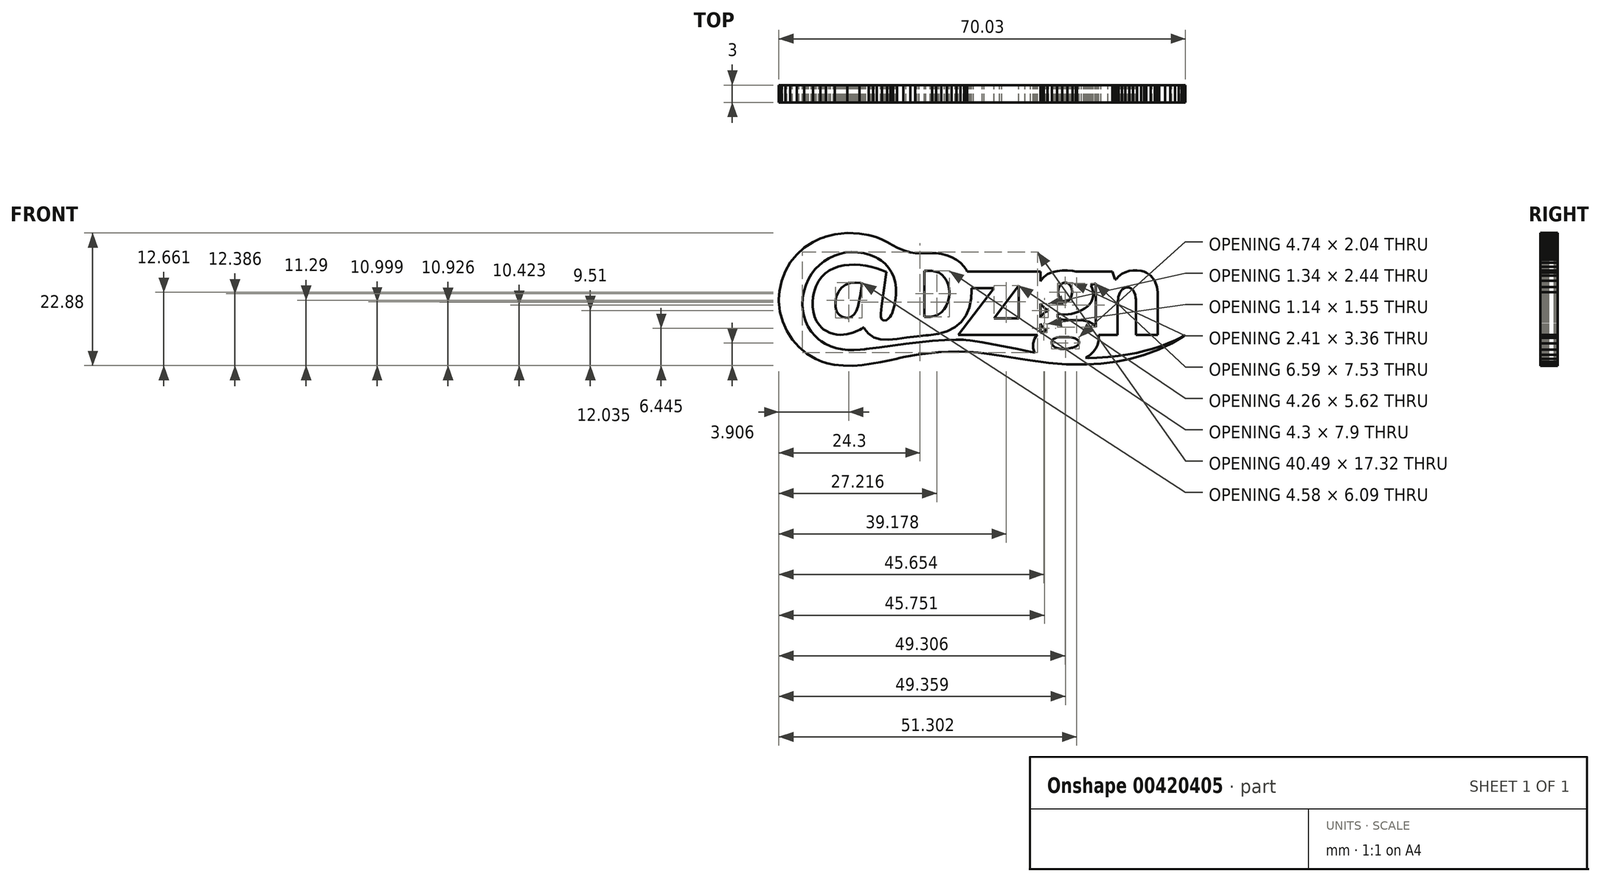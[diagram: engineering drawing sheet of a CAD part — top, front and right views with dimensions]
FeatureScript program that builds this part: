
annotation { "Feature Type Name" : "Feature", "Feature Type Description" : "" }
export const myFeature = defineFeature(function(context is Context, id is Id, definition is map)
    precondition{}
    {
        {
            var Q0;
            Q0=qCreatedBy(makeId("Front.planeOp"),FACE);
            var sketch = newSketch(context, id + "F0", { "sketchPlane" : qUnion([Q0])});
            skLineSegment(sketch, "E0", {"start": v(-17.71, 8.35) * mm, "end": v(-18.04, 6.17) * mm});
            skLineSegment(sketch, "E1", {"start": v(-18.04, 6.17) * mm, "end": v(-18.08, 5.96) * mm});
            skLineSegment(sketch, "E2", {"start": v(-18.08, 5.96) * mm, "end": v(-18.18, 5.3) * mm});
            skLineSegment(sketch, "E3", {"start": v(-18.18, 5.3) * mm, "end": v(-18.4, 4.37) * mm});
            skLineSegment(sketch, "E4", {"start": v(-18.4, 4.37) * mm, "end": v(-18.74, 3.5) * mm});
            skLineSegment(sketch, "E5", {"start": v(-18.74, 3.5) * mm, "end": v(-19.12, 2.94) * mm});
            skLineSegment(sketch, "E6", {"start": v(-19.12, 2.94) * mm, "end": v(-19.29, 2.8) * mm});
            skLineSegment(sketch, "E7", {"start": v(-19.29, 2.8) * mm, "end": v(-19.38, 2.71) * mm});
            skLineSegment(sketch, "E8", {"start": v(-19.38, 2.71) * mm, "end": v(-19.73, 2.52) * mm});
            skLineSegment(sketch, "E9", {"start": v(-19.73, 2.52) * mm, "end": v(-20.2, 2.4) * mm});
            skLineSegment(sketch, "E10", {"start": v(-20.2, 2.4) * mm, "end": v(-20.66, 2.41) * mm});
            skLineSegment(sketch, "E11", {"start": v(-20.66, 2.41) * mm, "end": v(-21.1, 2.55) * mm});
            skLineSegment(sketch, "E12", {"start": v(-21.1, 2.55) * mm, "end": v(-21.5, 2.8) * mm});
            skLineSegment(sketch, "E13", {"start": v(-21.5, 2.8) * mm, "end": v(-21.84, 3.13) * mm});
            skLineSegment(sketch, "E14", {"start": v(-21.84, 3.13) * mm, "end": v(-22.09, 3.55) * mm});
            skLineSegment(sketch, "E15", {"start": v(-22.09, 3.55) * mm, "end": v(-22.21, 3.9) * mm});
            skLineSegment(sketch, "E16", {"start": v(-22.21, 3.9) * mm, "end": v(-22.23, 4.02) * mm});
            skLineSegment(sketch, "E17", {"start": v(-22.23, 4.02) * mm, "end": v(-22.28, 4.28) * mm});
            skLineSegment(sketch, "E18", {"start": v(-22.28, 4.28) * mm, "end": v(-22.3, 5.09) * mm});
            skLineSegment(sketch, "E19", {"start": v(-22.3, 5.09) * mm, "end": v(-22.14, 6.05) * mm});
            skLineSegment(sketch, "E20", {"start": v(-22.14, 6.05) * mm, "end": v(-21.78, 6.88) * mm});
            skLineSegment(sketch, "E21", {"start": v(-21.78, 6.88) * mm, "end": v(-21.24, 7.56) * mm});
            skLineSegment(sketch, "E22", {"start": v(-21.24, 7.56) * mm, "end": v(-20.54, 8.07) * mm});
            skLineSegment(sketch, "E23", {"start": v(-20.54, 8.07) * mm, "end": v(-19.71, 8.38) * mm});
            skLineSegment(sketch, "E24", {"start": v(-19.71, 8.38) * mm, "end": v(-18.76, 8.48) * mm});
            skLineSegment(sketch, "E25", {"start": v(-18.76, 8.48) * mm, "end": v(-17.97, 8.4) * mm});
            skLineSegment(sketch, "E26", {"start": v(-17.97, 8.4) * mm, "end": v(-17.71, 8.35) * mm});
            skLineSegment(sketch, "E27", {"start": v(-16.97, -2.98) * mm, "end": v(-17.23, -3.02) * mm});
            skLineSegment(sketch, "E28", {"start": v(-17.23, -3.02) * mm, "end": v(-18.02, -3.1) * mm});
            skLineSegment(sketch, "E29", {"start": v(-18.02, -3.1) * mm, "end": v(-19.07, -3.14) * mm});
            skLineSegment(sketch, "E30", {"start": v(-19.07, -3.14) * mm, "end": v(-20.11, -3.13) * mm});
            skLineSegment(sketch, "E31", {"start": v(-20.11, -3.13) * mm, "end": v(-21.14, -3.02) * mm});
            skLineSegment(sketch, "E32", {"start": v(-21.14, -3.02) * mm, "end": v(-22.15, -2.82) * mm});
            skLineSegment(sketch, "E33", {"start": v(-22.15, -2.82) * mm, "end": v(-23.13, -2.5) * mm});
            skLineSegment(sketch, "E34", {"start": v(-23.13, -2.5) * mm, "end": v(-24.07, -2.06) * mm});
            skLineSegment(sketch, "E35", {"start": v(-24.07, -2.06) * mm, "end": v(-24.75, -1.64) * mm});
            skLineSegment(sketch, "E36", {"start": v(-24.75, -1.64) * mm, "end": v(-24.97, -1.48) * mm});
            skLineSegment(sketch, "E37", {"start": v(-24.97, -1.48) * mm, "end": v(-25.18, -1.31) * mm});
            skLineSegment(sketch, "E38", {"start": v(-25.18, -1.31) * mm, "end": v(-25.78, -0.77) * mm});
            skLineSegment(sketch, "E39", {"start": v(-25.78, -0.77) * mm, "end": v(-26.46, 0.03) * mm});
            skLineSegment(sketch, "E40", {"start": v(-26.46, 0.03) * mm, "end": v(-27.02, 0.9) * mm});
            skLineSegment(sketch, "E41", {"start": v(-27.02, 0.9) * mm, "end": v(-27.45, 1.83) * mm});
            skLineSegment(sketch, "E42", {"start": v(-27.45, 1.83) * mm, "end": v(-27.76, 2.8) * mm});
            skLineSegment(sketch, "E43", {"start": v(-27.76, 2.8) * mm, "end": v(-27.93, 3.83) * mm});
            skLineSegment(sketch, "E44", {"start": v(-27.93, 3.83) * mm, "end": v(-27.98, 4.88) * mm});
            skLineSegment(sketch, "E45", {"start": v(-27.98, 4.88) * mm, "end": v(-27.94, 5.68) * mm});
            skLineSegment(sketch, "E46", {"start": v(-27.94, 5.68) * mm, "end": v(-27.9, 5.94) * mm});
            skLineSegment(sketch, "E47", {"start": v(-27.9, 5.94) * mm, "end": v(-27.86, 6.22) * mm});
            skLineSegment(sketch, "E48", {"start": v(-27.86, 6.22) * mm, "end": v(-27.69, 7.05) * mm});
            skLineSegment(sketch, "E49", {"start": v(-27.69, 7.05) * mm, "end": v(-27.35, 8.1) * mm});
            skLineSegment(sketch, "E50", {"start": v(-27.35, 8.1) * mm, "end": v(-26.91, 9.08) * mm});
            skLineSegment(sketch, "E51", {"start": v(-26.91, 9.08) * mm, "end": v(-26.38, 9.97) * mm});
            skLineSegment(sketch, "E52", {"start": v(-26.38, 9.97) * mm, "end": v(-25.75, 10.8) * mm});
            skLineSegment(sketch, "E53", {"start": v(-25.75, 10.8) * mm, "end": v(-25.04, 11.52) * mm});
            skLineSegment(sketch, "E54", {"start": v(-25.04, 11.52) * mm, "end": v(-24.25, 12.15) * mm});
            skLineSegment(sketch, "E55", {"start": v(-24.25, 12.15) * mm, "end": v(-23.4, 12.69) * mm});
            skLineSegment(sketch, "E56", {"start": v(-23.4, 12.69) * mm, "end": v(-22.5, 13.12) * mm});
            skLineSegment(sketch, "E57", {"start": v(-22.5, 13.12) * mm, "end": v(-21.54, 13.44) * mm});
            skLineSegment(sketch, "E58", {"start": v(-21.54, 13.44) * mm, "end": v(-20.55, 13.65) * mm});
            skLineSegment(sketch, "E59", {"start": v(-20.55, 13.65) * mm, "end": v(-19.52, 13.74) * mm});
            skLineSegment(sketch, "E60", {"start": v(-19.52, 13.74) * mm, "end": v(-18.47, 13.7) * mm});
            skLineSegment(sketch, "E61", {"start": v(-18.47, 13.7) * mm, "end": v(-17.4, 13.53) * mm});
            skLineSegment(sketch, "E62", {"start": v(-17.4, 13.53) * mm, "end": v(-16.33, 13.23) * mm});
            skLineSegment(sketch, "E63", {"start": v(-16.33, 13.23) * mm, "end": v(-15.52, 12.9) * mm});
            skLineSegment(sketch, "E64", {"start": v(-15.52, 12.9) * mm, "end": v(-15.26, 12.78) * mm});
            skLineSegment(sketch, "E65", {"start": v(-15.26, 12.78) * mm, "end": v(-15.04, 12.68) * mm});
            skLineSegment(sketch, "E66", {"start": v(-15.04, 12.68) * mm, "end": v(-14.42, 12.3) * mm});
            skLineSegment(sketch, "E67", {"start": v(-14.42, 12.3) * mm, "end": v(-13.7, 11.7) * mm});
            skLineSegment(sketch, "E68", {"start": v(-13.7, 11.7) * mm, "end": v(-13.11, 11.02) * mm});
            skLineSegment(sketch, "E69", {"start": v(-13.11, 11.02) * mm, "end": v(-12.63, 10.25) * mm});
            skLineSegment(sketch, "E70", {"start": v(-12.63, 10.25) * mm, "end": v(-12.27, 9.42) * mm});
            skLineSegment(sketch, "E71", {"start": v(-12.27, 9.42) * mm, "end": v(-12.02, 8.54) * mm});
            skLineSegment(sketch, "E72", {"start": v(-12.02, 8.54) * mm, "end": v(-11.88, 7.6) * mm});
            skLineSegment(sketch, "E73", {"start": v(-11.88, 7.6) * mm, "end": v(-11.84, 6.9) * mm});
            skLineSegment(sketch, "E74", {"start": v(-11.84, 6.9) * mm, "end": v(-11.85, 6.65) * mm});
            skLineSegment(sketch, "E75", {"start": v(-11.85, 6.65) * mm, "end": v(-11.86, 6.34) * mm});
            skLineSegment(sketch, "E76", {"start": v(-11.86, 6.34) * mm, "end": v(-12.04, 4.77) * mm});
            skLineSegment(sketch, "E77", {"start": v(-12.04, 4.77) * mm, "end": v(-12.48, 3.24) * mm});
            skLineSegment(sketch, "E78", {"start": v(-12.48, 3.24) * mm, "end": v(-12.62, 2.96) * mm});
            skLineSegment(sketch, "E79", {"start": v(-12.62, 2.96) * mm, "end": v(-12.67, 2.85) * mm});
            skLineSegment(sketch, "E80", {"start": v(-12.67, 2.85) * mm, "end": v(-12.87, 2.55) * mm});
            skLineSegment(sketch, "E81", {"start": v(-12.87, 2.55) * mm, "end": v(-13.17, 2.23) * mm});
            skLineSegment(sketch, "E82", {"start": v(-13.17, 2.23) * mm, "end": v(-13.5, 2.02) * mm});
            skLineSegment(sketch, "E83", {"start": v(-13.5, 2.02) * mm, "end": v(-13.82, 1.93) * mm});
            skLineSegment(sketch, "E84", {"start": v(-13.82, 1.93) * mm, "end": v(-14.1, 1.98) * mm});
            skLineSegment(sketch, "E85", {"start": v(-14.1, 1.98) * mm, "end": v(-14.34, 2.19) * mm});
            skLineSegment(sketch, "E86", {"start": v(-14.34, 2.19) * mm, "end": v(-14.47, 2.56) * mm});
            skLineSegment(sketch, "E87", {"start": v(-14.47, 2.56) * mm, "end": v(-14.5, 2.98) * mm});
            skLineSegment(sketch, "E88", {"start": v(-14.5, 2.98) * mm, "end": v(-14.48, 3.11) * mm});
            skLineSegment(sketch, "E89", {"start": v(-14.48, 3.11) * mm, "end": v(-14.34, 4.43) * mm});
            skLineSegment(sketch, "E90", {"start": v(-14.34, 4.43) * mm, "end": v(-13.52, 10.3) * mm});
            skLineSegment(sketch, "E91", {"start": v(-13.52, 10.3) * mm, "end": v(-13.73, 10.4) * mm});
            skLineSegment(sketch, "E92", {"start": v(-13.73, 10.4) * mm, "end": v(-14.36, 10.64) * mm});
            skLineSegment(sketch, "E93", {"start": v(-14.36, 10.64) * mm, "end": v(-15.24, 10.94) * mm});
            skLineSegment(sketch, "E94", {"start": v(-15.24, 10.94) * mm, "end": v(-16.16, 11.18) * mm});
            skLineSegment(sketch, "E95", {"start": v(-16.16, 11.18) * mm, "end": v(-17.1, 11.37) * mm});
            skLineSegment(sketch, "E96", {"start": v(-17.1, 11.37) * mm, "end": v(-18.04, 11.5) * mm});
            skLineSegment(sketch, "E97", {"start": v(-18.04, 11.5) * mm, "end": v(-19, 11.55) * mm});
            skLineSegment(sketch, "E98", {"start": v(-19, 11.55) * mm, "end": v(-19.93, 11.53) * mm});
            skLineSegment(sketch, "E99", {"start": v(-19.93, 11.53) * mm, "end": v(-20.84, 11.43) * mm});
            skLineSegment(sketch, "E100", {"start": v(-20.84, 11.43) * mm, "end": v(-21.72, 11.23) * mm});
            skLineSegment(sketch, "E101", {"start": v(-21.72, 11.23) * mm, "end": v(-22.56, 10.94) * mm});
            skLineSegment(sketch, "E102", {"start": v(-22.56, 10.94) * mm, "end": v(-23.33, 10.55) * mm});
            skLineSegment(sketch, "E103", {"start": v(-23.33, 10.55) * mm, "end": v(-24.04, 10.05) * mm});
            skLineSegment(sketch, "E104", {"start": v(-24.04, 10.05) * mm, "end": v(-24.68, 9.43) * mm});
            skLineSegment(sketch, "E105", {"start": v(-24.68, 9.43) * mm, "end": v(-25.22, 8.7) * mm});
            skLineSegment(sketch, "E106", {"start": v(-25.22, 8.7) * mm, "end": v(-25.66, 7.83) * mm});
            skLineSegment(sketch, "E107", {"start": v(-25.66, 7.83) * mm, "end": v(-25.92, 7.08) * mm});
            skLineSegment(sketch, "E108", {"start": v(-25.92, 7.08) * mm, "end": v(-25.99, 6.83) * mm});
            skLineSegment(sketch, "E109", {"start": v(-25.99, 6.83) * mm, "end": v(-26.04, 6.62) * mm});
            skLineSegment(sketch, "E110", {"start": v(-26.04, 6.62) * mm, "end": v(-26.15, 6) * mm});
            skLineSegment(sketch, "E111", {"start": v(-26.15, 6) * mm, "end": v(-26.23, 5.15) * mm});
            skLineSegment(sketch, "E112", {"start": v(-26.23, 5.15) * mm, "end": v(-26.22, 4.3) * mm});
            skLineSegment(sketch, "E113", {"start": v(-26.22, 4.3) * mm, "end": v(-26.12, 3.44) * mm});
            skLineSegment(sketch, "E114", {"start": v(-26.12, 3.44) * mm, "end": v(-25.9, 2.62) * mm});
            skLineSegment(sketch, "E115", {"start": v(-25.9, 2.62) * mm, "end": v(-25.56, 1.85) * mm});
            skLineSegment(sketch, "E116", {"start": v(-25.56, 1.85) * mm, "end": v(-25.1, 1.15) * mm});
            skLineSegment(sketch, "E117", {"start": v(-25.1, 1.15) * mm, "end": v(-24.65, 0.68) * mm});
            skLineSegment(sketch, "E118", {"start": v(-24.65, 0.68) * mm, "end": v(-24.49, 0.54) * mm});
            skLineSegment(sketch, "E119", {"start": v(-24.49, 0.54) * mm, "end": v(-24.35, 0.43) * mm});
            skLineSegment(sketch, "E120", {"start": v(-24.35, 0.43) * mm, "end": v(-23.9, 0.13) * mm});
            skLineSegment(sketch, "E121", {"start": v(-23.9, 0.13) * mm, "end": v(-23.3, -0.17) * mm});
            skLineSegment(sketch, "E122", {"start": v(-23.3, -0.17) * mm, "end": v(-22.68, -0.37) * mm});
            skLineSegment(sketch, "E123", {"start": v(-22.68, -0.37) * mm, "end": v(-22.07, -0.49) * mm});
            skLineSegment(sketch, "E124", {"start": v(-22.07, -0.49) * mm, "end": v(-21.47, -0.52) * mm});
            skLineSegment(sketch, "E125", {"start": v(-21.47, -0.52) * mm, "end": v(-20.88, -0.5) * mm});
            skLineSegment(sketch, "E126", {"start": v(-20.88, -0.5) * mm, "end": v(-20.32, -0.42) * mm});
            skLineSegment(sketch, "E127", {"start": v(-20.32, -0.42) * mm, "end": v(-19.78, -0.3) * mm});
            skLineSegment(sketch, "E128", {"start": v(-19.78, -0.3) * mm, "end": v(-19.28, -0.15) * mm});
            skLineSegment(sketch, "E129", {"start": v(-19.28, -0.15) * mm, "end": v(-18.82, 0.02) * mm});
            skLineSegment(sketch, "E130", {"start": v(-18.82, 0.02) * mm, "end": v(-18.42, 0.2) * mm});
            skLineSegment(sketch, "E131", {"start": v(-18.42, 0.2) * mm, "end": v(-18.07, 0.36) * mm});
            skLineSegment(sketch, "E132", {"start": v(-18.07, 0.36) * mm, "end": v(-17.79, 0.51) * mm});
            skLineSegment(sketch, "E133", {"start": v(-17.79, 0.51) * mm, "end": v(-17.58, 0.64) * mm});
            skLineSegment(sketch, "E134", {"start": v(-17.58, 0.64) * mm, "end": v(-17.44, 0.72) * mm});
            skLineSegment(sketch, "E135", {"start": v(-17.44, 0.72) * mm, "end": v(-17.4, 0.75) * mm});
            skLineSegment(sketch, "E136", {"start": v(-17.4, 0.75) * mm, "end": v(-17.25, 0.46) * mm});
            skLineSegment(sketch, "E137", {"start": v(-17.25, 0.46) * mm, "end": v(-16.62, -0.32) * mm});
            skLineSegment(sketch, "E138", {"start": v(-16.62, -0.32) * mm, "end": v(-15.65, -0.98) * mm});
            skLineSegment(sketch, "E139", {"start": v(-15.65, -0.98) * mm, "end": v(-14.5, -1.3) * mm});
            skLineSegment(sketch, "E140", {"start": v(-14.5, -1.3) * mm, "end": v(-13.18, -1.35) * mm});
            skLineSegment(sketch, "E141", {"start": v(-13.18, -1.35) * mm, "end": v(-11.69, -1.23) * mm});
            skLineSegment(sketch, "E142", {"start": v(-11.69, -1.23) * mm, "end": v(-10.03, -1) * mm});
            skLineSegment(sketch, "E143", {"start": v(-10.03, -1) * mm, "end": v(-8.22, -0.77) * mm});
            skLineSegment(sketch, "E144", {"start": v(-8.22, -0.77) * mm, "end": v(-6.74, -0.63) * mm});
            skLineSegment(sketch, "E145", {"start": v(-6.74, -0.63) * mm, "end": v(-6.25, -0.6) * mm});
            skLineSegment(sketch, "E146", {"start": v(-6.25, -0.6) * mm, "end": v(-5.83, -0.57) * mm});
            skLineSegment(sketch, "E147", {"start": v(-5.83, -0.57) * mm, "end": v(-4.55, -0.38) * mm});
            skLineSegment(sketch, "E148", {"start": v(-4.55, -0.38) * mm, "end": v(-3.04, 0.08) * mm});
            skLineSegment(sketch, "E149", {"start": v(-3.04, 0.08) * mm, "end": v(-1.73, 0.76) * mm});
            skLineSegment(sketch, "E150", {"start": v(-1.73, 0.76) * mm, "end": v(-0.65, 1.68) * mm});
            skLineSegment(sketch, "E151", {"start": v(-0.65, 1.68) * mm, "end": v(0.2, 2.81) * mm});
            skLineSegment(sketch, "E152", {"start": v(0.2, 2.81) * mm, "end": v(0.8, 4.16) * mm});
            skLineSegment(sketch, "E153", {"start": v(0.8, 4.16) * mm, "end": v(1.12, 5.73) * mm});
            skLineSegment(sketch, "E154", {"start": v(1.12, 5.73) * mm, "end": v(1.18, 7.06) * mm});
            skLineSegment(sketch, "E155", {"start": v(1.18, 7.06) * mm, "end": v(1.15, 7.5) * mm});
            skLineSegment(sketch, "E156", {"start": v(1.15, 7.5) * mm, "end": v(5.02, 7.5) * mm});
            skLineSegment(sketch, "E157", {"start": v(5.02, 7.5) * mm, "end": v(-1.1, -0.55) * mm});
            skLineSegment(sketch, "E158", {"start": v(-1.1, -0.55) * mm, "end": v(12.5, -0.55) * mm});
            skLineSegment(sketch, "E159", {"start": v(12.5, -0.55) * mm, "end": v(12.35, -0.68) * mm});
            skLineSegment(sketch, "E160", {"start": v(12.35, -0.68) * mm, "end": v(12, -1.2) * mm});
            skLineSegment(sketch, "E161", {"start": v(12, -1.2) * mm, "end": v(11.76, -1.99) * mm});
            skLineSegment(sketch, "E162", {"start": v(11.76, -1.99) * mm, "end": v(11.79, -2.81) * mm});
            skLineSegment(sketch, "E163", {"start": v(11.79, -2.81) * mm, "end": v(11.97, -3.4) * mm});
            skLineSegment(sketch, "E164", {"start": v(11.97, -3.4) * mm, "end": v(12.07, -3.59) * mm});
            skLineSegment(sketch, "E165", {"start": v(12.07, -3.59) * mm, "end": v(11.31, -3.44) * mm});
            skLineSegment(sketch, "E166", {"start": v(11.31, -3.44) * mm, "end": v(9.04, -2.98) * mm});
            skLineSegment(sketch, "E167", {"start": v(9.04, -2.98) * mm, "end": v(5.97, -2.36) * mm});
            skLineSegment(sketch, "E168", {"start": v(5.97, -2.36) * mm, "end": v(2.98, -1.82) * mm});
            skLineSegment(sketch, "E169", {"start": v(2.98, -1.82) * mm, "end": v(0.9, -1.51) * mm});
            skLineSegment(sketch, "E170", {"start": v(0.9, -1.51) * mm, "end": v(0.2, -1.44) * mm});
            skLineSegment(sketch, "E171", {"start": v(0.2, -1.44) * mm, "end": v(-0.23, -1.4) * mm});
            skLineSegment(sketch, "E172", {"start": v(-0.23, -1.4) * mm, "end": v(-1.54, -1.36) * mm});
            skLineSegment(sketch, "E173", {"start": v(-1.54, -1.36) * mm, "end": v(-3.5, -1.41) * mm});
            skLineSegment(sketch, "E174", {"start": v(-3.5, -1.41) * mm, "end": v(-5.6, -1.56) * mm});
            skLineSegment(sketch, "E175", {"start": v(-5.6, -1.56) * mm, "end": v(-7.83, -1.79) * mm});
            skLineSegment(sketch, "E176", {"start": v(-7.83, -1.79) * mm, "end": v(-10.13, -2.07) * mm});
            skLineSegment(sketch, "E177", {"start": v(-10.13, -2.07) * mm, "end": v(-12.45, -2.38) * mm});
            skLineSegment(sketch, "E178", {"start": v(-12.45, -2.38) * mm, "end": v(-14.74, -2.7) * mm});
            skLineSegment(sketch, "E179", {"start": v(-14.74, -2.7) * mm, "end": v(-16.41, -2.91) * mm});
            skLineSegment(sketch, "E180", {"start": v(-16.41, -2.91) * mm, "end": v(-16.97, -2.98) * mm});
            skLineSegment(sketch, "E181", {"start": v(-6.98, 10.49) * mm, "end": v(-5.86, 10.49) * mm});
            skLineSegment(sketch, "E182", {"start": v(-5.86, 10.49) * mm, "end": v(-5.68, 10.49) * mm});
            skLineSegment(sketch, "E183", {"start": v(-5.68, 10.49) * mm, "end": v(-5.1, 10.4) * mm});
            skLineSegment(sketch, "E184", {"start": v(-5.1, 10.4) * mm, "end": v(-4.46, 10.17) * mm});
            skLineSegment(sketch, "E185", {"start": v(-4.46, 10.17) * mm, "end": v(-3.9, 9.8) * mm});
            skLineSegment(sketch, "E186", {"start": v(-3.9, 9.8) * mm, "end": v(-3.46, 9.32) * mm});
            skLineSegment(sketch, "E187", {"start": v(-3.46, 9.32) * mm, "end": v(-3.12, 8.75) * mm});
            skLineSegment(sketch, "E188", {"start": v(-3.12, 8.75) * mm, "end": v(-2.87, 8.1) * mm});
            skLineSegment(sketch, "E189", {"start": v(-2.87, 8.1) * mm, "end": v(-2.72, 7.42) * mm});
            skLineSegment(sketch, "E190", {"start": v(-2.72, 7.42) * mm, "end": v(-2.67, 6.9) * mm});
            skLineSegment(sketch, "E191", {"start": v(-2.67, 6.9) * mm, "end": v(-2.67, 6.71) * mm});
            skLineSegment(sketch, "E192", {"start": v(-2.67, 6.71) * mm, "end": v(-2.67, 6.52) * mm});
            skLineSegment(sketch, "E193", {"start": v(-2.67, 6.52) * mm, "end": v(-2.73, 5.95) * mm});
            skLineSegment(sketch, "E194", {"start": v(-2.73, 5.95) * mm, "end": v(-2.9, 5.21) * mm});
            skLineSegment(sketch, "E195", {"start": v(-2.9, 5.21) * mm, "end": v(-3.16, 4.52) * mm});
            skLineSegment(sketch, "E196", {"start": v(-3.16, 4.52) * mm, "end": v(-3.54, 3.89) * mm});
            skLineSegment(sketch, "E197", {"start": v(-3.54, 3.89) * mm, "end": v(-4.03, 3.36) * mm});
            skLineSegment(sketch, "E198", {"start": v(-4.03, 3.36) * mm, "end": v(-4.63, 2.94) * mm});
            skLineSegment(sketch, "E199", {"start": v(-4.63, 2.94) * mm, "end": v(-5.33, 2.68) * mm});
            skLineSegment(sketch, "E200", {"start": v(-5.33, 2.68) * mm, "end": v(-5.93, 2.58) * mm});
            skLineSegment(sketch, "E201", {"start": v(-5.93, 2.58) * mm, "end": v(-6.13, 2.58) * mm});
            skLineSegment(sketch, "E202", {"start": v(-6.13, 2.58) * mm, "end": v(-6.98, 2.58) * mm});
            skLineSegment(sketch, "E203", {"start": v(-6.98, 2.58) * mm, "end": v(-6.98, 10.49) * mm});
            skLineSegment(sketch, "E204", {"start": v(9.27, 2.34) * mm, "end": v(5, 2.34) * mm});
            skLineSegment(sketch, "E205", {"start": v(5, 2.34) * mm, "end": v(9.27, 7.96) * mm});
            skLineSegment(sketch, "E206", {"start": v(9.27, 7.96) * mm, "end": v(9.27, 2.34) * mm});
            skLineSegment(sketch, "E207", {"start": v(13.1, 4.78) * mm, "end": v(13.31, 4.5) * mm});
            skLineSegment(sketch, "E208", {"start": v(13.31, 4.5) * mm, "end": v(13.62, 4.19) * mm});
            skLineSegment(sketch, "E209", {"start": v(13.62, 4.19) * mm, "end": v(13.98, 3.92) * mm});
            skLineSegment(sketch, "E210", {"start": v(13.98, 3.92) * mm, "end": v(14.28, 3.75) * mm});
            skLineSegment(sketch, "E211", {"start": v(14.28, 3.75) * mm, "end": v(14.38, 3.7) * mm});
            skLineSegment(sketch, "E212", {"start": v(14.38, 3.7) * mm, "end": v(14.28, 3.65) * mm});
            skLineSegment(sketch, "E213", {"start": v(14.28, 3.65) * mm, "end": v(13.99, 3.46) * mm});
            skLineSegment(sketch, "E214", {"start": v(13.99, 3.46) * mm, "end": v(13.6, 3.18) * mm});
            skLineSegment(sketch, "E215", {"start": v(13.6, 3.18) * mm, "end": v(13.27, 2.85) * mm});
            skLineSegment(sketch, "E216", {"start": v(13.27, 2.85) * mm, "end": v(13.08, 2.55) * mm});
            skLineSegment(sketch, "E217", {"start": v(13.08, 2.55) * mm, "end": v(13.04, 2.44) * mm});
            skLineSegment(sketch, "E218", {"start": v(13.04, 2.44) * mm, "end": v(13.04, 4.88) * mm});
            skLineSegment(sketch, "E219", {"start": v(15.42, -1.16) * mm, "end": v(15.81, -1) * mm});
            skLineSegment(sketch, "E220", {"start": v(15.81, -1) * mm, "end": v(16.24, -0.92) * mm});
            skLineSegment(sketch, "E221", {"start": v(16.24, -0.92) * mm, "end": v(16.38, -0.92) * mm});
            skLineSegment(sketch, "E222", {"start": v(16.38, -0.92) * mm, "end": v(17.86, -0.92) * mm});
            skLineSegment(sketch, "E223", {"start": v(17.86, -0.92) * mm, "end": v(18, -0.92) * mm});
            skLineSegment(sketch, "E224", {"start": v(18, -0.92) * mm, "end": v(18.44, -0.98) * mm});
            skLineSegment(sketch, "E225", {"start": v(18.44, -0.98) * mm, "end": v(18.95, -1.13) * mm});
            skLineSegment(sketch, "E226", {"start": v(18.95, -1.13) * mm, "end": v(19.35, -1.35) * mm});
            skLineSegment(sketch, "E227", {"start": v(19.35, -1.35) * mm, "end": v(19.6, -1.62) * mm});
            skLineSegment(sketch, "E228", {"start": v(19.6, -1.62) * mm, "end": v(19.7, -1.92) * mm});
            skLineSegment(sketch, "E229", {"start": v(19.7, -1.92) * mm, "end": v(19.56, -2.22) * mm});
            skLineSegment(sketch, "E230", {"start": v(19.56, -2.22) * mm, "end": v(19.19, -2.5) * mm});
            skLineSegment(sketch, "E231", {"start": v(19.19, -2.5) * mm, "end": v(18.7, -2.7) * mm});
            skLineSegment(sketch, "E232", {"start": v(18.7, -2.7) * mm, "end": v(18.53, -2.75) * mm});
            skLineSegment(sketch, "E233", {"start": v(18.53, -2.75) * mm, "end": v(18.37, -2.8) * mm});
            skLineSegment(sketch, "E234", {"start": v(18.37, -2.8) * mm, "end": v(17.87, -2.9) * mm});
            skLineSegment(sketch, "E235", {"start": v(17.87, -2.9) * mm, "end": v(17.17, -2.96) * mm});
            skLineSegment(sketch, "E236", {"start": v(17.17, -2.96) * mm, "end": v(16.47, -2.94) * mm});
            skLineSegment(sketch, "E237", {"start": v(16.47, -2.94) * mm, "end": v(15.97, -2.86) * mm});
            skLineSegment(sketch, "E238", {"start": v(15.97, -2.86) * mm, "end": v(15.8, -2.81) * mm});
            skLineSegment(sketch, "E239", {"start": v(15.8, -2.81) * mm, "end": v(15.74, -2.8) * mm});
            skLineSegment(sketch, "E240", {"start": v(15.74, -2.8) * mm, "end": v(15.54, -2.7) * mm});
            skLineSegment(sketch, "E241", {"start": v(15.54, -2.7) * mm, "end": v(15.3, -2.54) * mm});
            skLineSegment(sketch, "E242", {"start": v(15.3, -2.54) * mm, "end": v(15.12, -2.35) * mm});
            skLineSegment(sketch, "E243", {"start": v(15.12, -2.35) * mm, "end": v(15, -2.13) * mm});
            skLineSegment(sketch, "E244", {"start": v(15, -2.13) * mm, "end": v(14.95, -1.9) * mm});
            skLineSegment(sketch, "E245", {"start": v(14.95, -1.9) * mm, "end": v(14.98, -1.66) * mm});
            skLineSegment(sketch, "E246", {"start": v(14.98, -1.66) * mm, "end": v(15.1, -1.42) * mm});
            skLineSegment(sketch, "E247", {"start": v(15.1, -1.42) * mm, "end": v(15.28, -1.25) * mm});
            skLineSegment(sketch, "E248", {"start": v(16.08, 3.07) * mm, "end": v(16.21, 3.05) * mm});
            skLineSegment(sketch, "E249", {"start": v(16.21, 3.05) * mm, "end": v(16.61, 3) * mm});
            skLineSegment(sketch, "E250", {"start": v(16.61, 3) * mm, "end": v(17.18, 2.97) * mm});
            skLineSegment(sketch, "E251", {"start": v(17.18, 2.97) * mm, "end": v(17.77, 3) * mm});
            skLineSegment(sketch, "E252", {"start": v(17.77, 3) * mm, "end": v(18.37, 3.1) * mm});
            skLineSegment(sketch, "E253", {"start": v(18.37, 3.1) * mm, "end": v(18.97, 3.25) * mm});
            skLineSegment(sketch, "E254", {"start": v(18.97, 3.25) * mm, "end": v(19.55, 3.45) * mm});
            skLineSegment(sketch, "E255", {"start": v(19.55, 3.45) * mm, "end": v(20.1, 3.7) * mm});
            skLineSegment(sketch, "E256", {"start": v(20.1, 3.7) * mm, "end": v(20.62, 4) * mm});
            skLineSegment(sketch, "E257", {"start": v(20.62, 4) * mm, "end": v(21.08, 4.35) * mm});
            skLineSegment(sketch, "E258", {"start": v(21.08, 4.35) * mm, "end": v(21.47, 4.75) * mm});
            skLineSegment(sketch, "E259", {"start": v(21.47, 4.75) * mm, "end": v(21.78, 5.2) * mm});
            skLineSegment(sketch, "E260", {"start": v(21.78, 5.2) * mm, "end": v(22, 5.68) * mm});
            skLineSegment(sketch, "E261", {"start": v(22, 5.68) * mm, "end": v(22.11, 6.2) * mm});
            skLineSegment(sketch, "E262", {"start": v(22.11, 6.2) * mm, "end": v(22.1, 6.77) * mm});
            skLineSegment(sketch, "E263", {"start": v(22.1, 6.77) * mm, "end": v(21.97, 7.37) * mm});
            skLineSegment(sketch, "E264", {"start": v(21.97, 7.37) * mm, "end": v(21.76, 7.86) * mm});
            skLineSegment(sketch, "E265", {"start": v(21.76, 7.86) * mm, "end": v(21.68, 8) * mm});
            skLineSegment(sketch, "E266", {"start": v(21.68, 8) * mm, "end": v(22.56, 8.34) * mm});
            skLineSegment(sketch, "E267", {"start": v(22.56, 8.34) * mm, "end": v(22.56, 0.8) * mm});
            skLineSegment(sketch, "E268", {"start": v(22.56, 0.8) * mm, "end": v(22.45, 0.96) * mm});
            skLineSegment(sketch, "E269", {"start": v(22.45, 0.96) * mm, "end": v(22.04, 1.34) * mm});
            skLineSegment(sketch, "E270", {"start": v(22.04, 1.34) * mm, "end": v(21.34, 1.72) * mm});
            skLineSegment(sketch, "E271", {"start": v(21.34, 1.72) * mm, "end": v(20.46, 1.95) * mm});
            skLineSegment(sketch, "E272", {"start": v(20.46, 1.95) * mm, "end": v(19.66, 2.02) * mm});
            skLineSegment(sketch, "E273", {"start": v(19.66, 2.02) * mm, "end": v(19.4, 2.02) * mm});
            skLineSegment(sketch, "E274", {"start": v(19.4, 2.02) * mm, "end": v(17.58, 2.02) * mm});
            skLineSegment(sketch, "E275", {"start": v(17.58, 2.02) * mm, "end": v(17.51, 2.02) * mm});
            skLineSegment(sketch, "E276", {"start": v(17.51, 2.02) * mm, "end": v(17.32, 2.03) * mm});
            skLineSegment(sketch, "E277", {"start": v(17.32, 2.03) * mm, "end": v(17, 2.05) * mm});
            skLineSegment(sketch, "E278", {"start": v(17, 2.05) * mm, "end": v(16.7, 2.1) * mm});
            skLineSegment(sketch, "E279", {"start": v(16.7, 2.1) * mm, "end": v(16.4, 2.17) * mm});
            skLineSegment(sketch, "E280", {"start": v(16.4, 2.17) * mm, "end": v(16.15, 2.3) * mm});
            skLineSegment(sketch, "E281", {"start": v(16.15, 2.3) * mm, "end": v(16, 2.49) * mm});
            skLineSegment(sketch, "E282", {"start": v(16, 2.49) * mm, "end": v(15.97, 2.74) * mm});
            skLineSegment(sketch, "E283", {"start": v(15.97, 2.74) * mm, "end": v(16.04, 3) * mm});
            skLineSegment(sketch, "E284", {"start": v(16.04, 3) * mm, "end": v(16.08, 3.07) * mm});
            skLineSegment(sketch, "E285", {"start": v(17.29, 8.49) * mm, "end": v(17.42, 8.49) * mm});
            skLineSegment(sketch, "E286", {"start": v(17.42, 8.49) * mm, "end": v(17.8, 8.34) * mm});
            skLineSegment(sketch, "E287", {"start": v(17.8, 8.34) * mm, "end": v(18.18, 7.96) * mm});
            skLineSegment(sketch, "E288", {"start": v(18.18, 7.96) * mm, "end": v(18.4, 7.43) * mm});
            skLineSegment(sketch, "E289", {"start": v(18.4, 7.43) * mm, "end": v(18.47, 6.81) * mm});
            skLineSegment(sketch, "E290", {"start": v(18.47, 6.81) * mm, "end": v(18.4, 6.2) * mm});
            skLineSegment(sketch, "E291", {"start": v(18.4, 6.2) * mm, "end": v(18.17, 5.66) * mm});
            skLineSegment(sketch, "E292", {"start": v(18.17, 5.66) * mm, "end": v(17.8, 5.28) * mm});
            skLineSegment(sketch, "E293", {"start": v(17.8, 5.28) * mm, "end": v(17.41, 5.13) * mm});
            skLineSegment(sketch, "E294", {"start": v(17.41, 5.13) * mm, "end": v(17.29, 5.13) * mm});
            skLineSegment(sketch, "E295", {"start": v(17.29, 5.13) * mm, "end": v(17.15, 5.13) * mm});
            skLineSegment(sketch, "E296", {"start": v(17.15, 5.13) * mm, "end": v(16.75, 5.27) * mm});
            skLineSegment(sketch, "E297", {"start": v(16.75, 5.27) * mm, "end": v(16.37, 5.65) * mm});
            skLineSegment(sketch, "E298", {"start": v(16.37, 5.65) * mm, "end": v(16.14, 6.2) * mm});
            skLineSegment(sketch, "E299", {"start": v(16.14, 6.2) * mm, "end": v(16.06, 6.8) * mm});
            skLineSegment(sketch, "E300", {"start": v(16.06, 6.8) * mm, "end": v(16.14, 7.42) * mm});
            skLineSegment(sketch, "E301", {"start": v(16.14, 7.42) * mm, "end": v(16.37, 7.96) * mm});
            skLineSegment(sketch, "E302", {"start": v(16.37, 7.96) * mm, "end": v(16.75, 8.34) * mm});
            skLineSegment(sketch, "E303", {"start": v(16.75, 8.34) * mm, "end": v(17.15, 8.49) * mm});
            skLineSegment(sketch, "E304", {"start": v(17.15, 8.49) * mm, "end": v(17.29, 8.49) * mm});
            skLineSegment(sketch, "E305", {"start": v(13.04, 1.37) * mm, "end": v(13.08, 1.28) * mm});
            skLineSegment(sketch, "E306", {"start": v(13.08, 1.28) * mm, "end": v(13.24, 1.01) * mm});
            skLineSegment(sketch, "E307", {"start": v(13.24, 1.01) * mm, "end": v(13.5, 0.7) * mm});
            skLineSegment(sketch, "E308", {"start": v(13.5, 0.7) * mm, "end": v(13.82, 0.44) * mm});
            skLineSegment(sketch, "E309", {"start": v(13.82, 0.44) * mm, "end": v(14.1, 0.28) * mm});
            skLineSegment(sketch, "E310", {"start": v(14.1, 0.28) * mm, "end": v(14.19, 0.24) * mm});
            skLineSegment(sketch, "E311", {"start": v(14.19, 0.24) * mm, "end": v(14.08, 0.21) * mm});
            skLineSegment(sketch, "E312", {"start": v(14.08, 0.21) * mm, "end": v(13.57, 0.06) * mm});
            skLineSegment(sketch, "E313", {"start": v(13.57, 0.06) * mm, "end": v(13.12, -0.14) * mm});
            skLineSegment(sketch, "E314", {"start": v(13.12, -0.14) * mm, "end": v(13.04, -0.18) * mm});
            skLineSegment(sketch, "E315", {"start": v(13.04, -0.18) * mm, "end": v(13.04, 1.37) * mm});
            skLineSegment(sketch, "E316", {"start": v(23.04, -0.55) * mm, "end": v(26.33, -0.55) * mm});
            skLineSegment(sketch, "E317", {"start": v(26.33, -0.55) * mm, "end": v(26.33, 4.24) * mm});
            skLineSegment(sketch, "E318", {"start": v(26.33, 4.24) * mm, "end": v(26.33, 4.44) * mm});
            skLineSegment(sketch, "E319", {"start": v(26.33, 4.44) * mm, "end": v(26.34, 5.07) * mm});
            skLineSegment(sketch, "E320", {"start": v(26.34, 5.07) * mm, "end": v(26.44, 5.98) * mm});
            skLineSegment(sketch, "E321", {"start": v(26.44, 5.98) * mm, "end": v(26.73, 6.82) * mm});
            skLineSegment(sketch, "E322", {"start": v(26.73, 6.82) * mm, "end": v(27.14, 7.32) * mm});
            skLineSegment(sketch, "E323", {"start": v(27.14, 7.32) * mm, "end": v(27.31, 7.42) * mm});
            skLineSegment(sketch, "E324", {"start": v(27.31, 7.42) * mm, "end": v(27.43, 7.49) * mm});
            skLineSegment(sketch, "E325", {"start": v(27.43, 7.49) * mm, "end": v(27.84, 7.63) * mm});
            skLineSegment(sketch, "E326", {"start": v(27.84, 7.63) * mm, "end": v(28.3, 7.63) * mm});
            skLineSegment(sketch, "E327", {"start": v(28.3, 7.63) * mm, "end": v(28.66, 7.48) * mm});
            skLineSegment(sketch, "E328", {"start": v(28.66, 7.48) * mm, "end": v(28.95, 7.19) * mm});
            skLineSegment(sketch, "E329", {"start": v(28.95, 7.19) * mm, "end": v(29.18, 6.8) * mm});
            skLineSegment(sketch, "E330", {"start": v(29.18, 6.8) * mm, "end": v(29.33, 6.36) * mm});
            skLineSegment(sketch, "E331", {"start": v(29.33, 6.36) * mm, "end": v(29.42, 5.88) * mm});
            skLineSegment(sketch, "E332", {"start": v(29.42, 5.88) * mm, "end": v(29.45, 5.53) * mm});
            skLineSegment(sketch, "E333", {"start": v(29.45, 5.53) * mm, "end": v(29.45, 5.4) * mm});
            skLineSegment(sketch, "E334", {"start": v(29.45, 5.4) * mm, "end": v(29.45, -0.56) * mm});
            skLineSegment(sketch, "E335", {"start": v(29.45, -0.56) * mm, "end": v(33.23, -0.56) * mm});
            skLineSegment(sketch, "E336", {"start": v(33.23, -0.56) * mm, "end": v(33.23, 6.55) * mm});
            skLineSegment(sketch, "E337", {"start": v(33.23, 6.55) * mm, "end": v(33.23, 6.84) * mm});
            skLineSegment(sketch, "E338", {"start": v(33.23, 6.84) * mm, "end": v(33.1, 7.73) * mm});
            skLineSegment(sketch, "E339", {"start": v(33.1, 7.73) * mm, "end": v(32.7, 8.8) * mm});
            skLineSegment(sketch, "E340", {"start": v(32.7, 8.8) * mm, "end": v(32.02, 9.7) * mm});
            skLineSegment(sketch, "E341", {"start": v(32.02, 9.7) * mm, "end": v(31.27, 10.2) * mm});
            skLineSegment(sketch, "E342", {"start": v(31.27, 10.2) * mm, "end": v(31, 10.3) * mm});
            skLineSegment(sketch, "E343", {"start": v(31, 10.3) * mm, "end": v(30.85, 10.36) * mm});
            skLineSegment(sketch, "E344", {"start": v(30.85, 10.36) * mm, "end": v(30.37, 10.49) * mm});
            skLineSegment(sketch, "E345", {"start": v(30.37, 10.49) * mm, "end": v(29.69, 10.58) * mm});
            skLineSegment(sketch, "E346", {"start": v(29.69, 10.58) * mm, "end": v(29, 10.57) * mm});
            skLineSegment(sketch, "E347", {"start": v(29, 10.57) * mm, "end": v(28.3, 10.47) * mm});
            skLineSegment(sketch, "E348", {"start": v(28.3, 10.47) * mm, "end": v(27.64, 10.27) * mm});
            skLineSegment(sketch, "E349", {"start": v(27.64, 10.27) * mm, "end": v(27.04, 9.96) * mm});
            skLineSegment(sketch, "E350", {"start": v(27.04, 9.96) * mm, "end": v(26.51, 9.55) * mm});
            skLineSegment(sketch, "E351", {"start": v(26.51, 9.55) * mm, "end": v(26.18, 9.16) * mm});
            skLineSegment(sketch, "E352", {"start": v(26.18, 9.16) * mm, "end": v(26.09, 9.02) * mm});
            skLineSegment(sketch, "E353", {"start": v(26.09, 9.02) * mm, "end": v(25.86, 9.02) * mm});
            skLineSegment(sketch, "E354", {"start": v(25.86, 9.02) * mm, "end": v(25.4, 10.37) * mm});
            skLineSegment(sketch, "E355", {"start": v(25.4, 10.37) * mm, "end": v(19.35, 10.37) * mm});
            skLineSegment(sketch, "E356", {"start": v(19.35, 10.37) * mm, "end": v(19.14, 10.4) * mm});
            skLineSegment(sketch, "E357", {"start": v(19.14, 10.4) * mm, "end": v(18.53, 10.48) * mm});
            skLineSegment(sketch, "E358", {"start": v(18.53, 10.48) * mm, "end": v(17.66, 10.55) * mm});
            skLineSegment(sketch, "E359", {"start": v(17.66, 10.55) * mm, "end": v(16.76, 10.56) * mm});
            skLineSegment(sketch, "E360", {"start": v(16.76, 10.56) * mm, "end": v(15.87, 10.47) * mm});
            skLineSegment(sketch, "E361", {"start": v(15.87, 10.47) * mm, "end": v(15.03, 10.26) * mm});
            skLineSegment(sketch, "E362", {"start": v(15.03, 10.26) * mm, "end": v(14.25, 9.92) * mm});
            skLineSegment(sketch, "E363", {"start": v(14.25, 9.92) * mm, "end": v(13.57, 9.42) * mm});
            skLineSegment(sketch, "E364", {"start": v(13.57, 9.42) * mm, "end": v(13.13, 8.92) * mm});
            skLineSegment(sketch, "E365", {"start": v(13.13, 8.92) * mm, "end": v(13.02, 8.73) * mm});
            skLineSegment(sketch, "E366", {"start": v(13.02, 8.73) * mm, "end": v(13.02, 10.37) * mm});
            skLineSegment(sketch, "E367", {"start": v(13.02, 10.37) * mm, "end": v(0.42, 10.37) * mm});
            skLineSegment(sketch, "E368", {"start": v(0.42, 10.37) * mm, "end": v(0.3, 10.58) * mm});
            skLineSegment(sketch, "E369", {"start": v(0.3, 10.58) * mm, "end": v(-0.1, 11.18) * mm});
            skLineSegment(sketch, "E370", {"start": v(-0.1, 11.18) * mm, "end": v(-0.74, 11.87) * mm});
            skLineSegment(sketch, "E371", {"start": v(-0.74, 11.87) * mm, "end": v(-1.46, 12.42) * mm});
            skLineSegment(sketch, "E372", {"start": v(-1.46, 12.42) * mm, "end": v(-2.27, 12.85) * mm});
            skLineSegment(sketch, "E373", {"start": v(-2.27, 12.85) * mm, "end": v(-3.13, 13.17) * mm});
            skLineSegment(sketch, "E374", {"start": v(-3.13, 13.17) * mm, "end": v(-4.04, 13.4) * mm});
            skLineSegment(sketch, "E375", {"start": v(-4.04, 13.4) * mm, "end": v(-4.97, 13.52) * mm});
            skLineSegment(sketch, "E376", {"start": v(-4.97, 13.52) * mm, "end": v(-5.67, 13.56) * mm});
            skLineSegment(sketch, "E377", {"start": v(-5.67, 13.56) * mm, "end": v(-5.9, 13.56) * mm});
            skLineSegment(sketch, "E378", {"start": v(-5.9, 13.56) * mm, "end": v(-8.3, 13.56) * mm});
            skLineSegment(sketch, "E379", {"start": v(-8.3, 13.56) * mm, "end": v(-8.57, 13.56) * mm});
            skLineSegment(sketch, "E380", {"start": v(-8.57, 13.56) * mm, "end": v(-9.4, 13.69) * mm});
            skLineSegment(sketch, "E381", {"start": v(-9.4, 13.69) * mm, "end": v(-10.56, 14.03) * mm});
            skLineSegment(sketch, "E382", {"start": v(-10.56, 14.03) * mm, "end": v(-11.68, 14.5) * mm});
            skLineSegment(sketch, "E383", {"start": v(-11.68, 14.5) * mm, "end": v(-12.4, 14.87) * mm});
            skLineSegment(sketch, "E384", {"start": v(-12.4, 14.87) * mm, "end": v(-12.63, 15) * mm});
            skLineSegment(sketch, "E385", {"start": v(-12.63, 15) * mm, "end": v(-12.82, 15.12) * mm});
            skLineSegment(sketch, "E386", {"start": v(-12.82, 15.12) * mm, "end": v(-13.42, 15.46) * mm});
            skLineSegment(sketch, "E387", {"start": v(-13.42, 15.46) * mm, "end": v(-14.28, 15.89) * mm});
            skLineSegment(sketch, "E388", {"start": v(-14.28, 15.89) * mm, "end": v(-15.17, 16.26) * mm});
            skLineSegment(sketch, "E389", {"start": v(-15.17, 16.26) * mm, "end": v(-15.81, 16.49) * mm});
            skLineSegment(sketch, "E390", {"start": v(-15.81, 16.49) * mm, "end": v(-16.03, 16.55) * mm});
            skLineSegment(sketch, "E391", {"start": v(-16.03, 16.55) * mm, "end": v(-16.55, 16.68) * mm});
            skLineSegment(sketch, "E392", {"start": v(-16.55, 16.68) * mm, "end": v(-18.12, 16.93) * mm});
            skLineSegment(sketch, "E393", {"start": v(-18.12, 16.93) * mm, "end": v(-20.26, 17.03) * mm});
            skLineSegment(sketch, "E394", {"start": v(-20.26, 17.03) * mm, "end": v(-22.38, 16.8) * mm});
            skLineSegment(sketch, "E395", {"start": v(-22.38, 16.8) * mm, "end": v(-23.94, 16.42) * mm});
            skLineSegment(sketch, "E396", {"start": v(-23.94, 16.42) * mm, "end": v(-24.44, 16.24) * mm});
            skLineSegment(sketch, "E397", {"start": v(-24.44, 16.24) * mm, "end": v(-24.87, 16.08) * mm});
            skLineSegment(sketch, "E398", {"start": v(-24.87, 16.08) * mm, "end": v(-26.14, 15.46) * mm});
            skLineSegment(sketch, "E399", {"start": v(-26.14, 15.46) * mm, "end": v(-27.65, 14.47) * mm});
            skLineSegment(sketch, "E400", {"start": v(-27.65, 14.47) * mm, "end": v(-28.97, 13.29) * mm});
            skLineSegment(sketch, "E401", {"start": v(-28.97, 13.29) * mm, "end": v(-30.06, 11.93) * mm});
            skLineSegment(sketch, "E402", {"start": v(-30.06, 11.93) * mm, "end": v(-30.93, 10.42) * mm});
            skLineSegment(sketch, "E403", {"start": v(-30.93, 10.42) * mm, "end": v(-31.56, 8.78) * mm});
            skLineSegment(sketch, "E404", {"start": v(-31.56, 8.78) * mm, "end": v(-31.93, 7.02) * mm});
            skLineSegment(sketch, "E405", {"start": v(-31.93, 7.02) * mm, "end": v(-32.04, 5.64) * mm});
            skLineSegment(sketch, "E406", {"start": v(-32.04, 5.64) * mm, "end": v(-32.03, 5.17) * mm});
            skLineSegment(sketch, "E407", {"start": v(-32.03, 5.17) * mm, "end": v(-32.02, 4.74) * mm});
            skLineSegment(sketch, "E408", {"start": v(-32.02, 4.74) * mm, "end": v(-31.85, 3.44) * mm});
            skLineSegment(sketch, "E409", {"start": v(-31.85, 3.44) * mm, "end": v(-31.38, 1.75) * mm});
            skLineSegment(sketch, "E410", {"start": v(-31.38, 1.75) * mm, "end": v(-30.66, 0.14) * mm});
            skLineSegment(sketch, "E411", {"start": v(-30.66, 0.14) * mm, "end": v(-29.7, -1.35) * mm});
            skLineSegment(sketch, "E412", {"start": v(-29.7, -1.35) * mm, "end": v(-28.55, -2.67) * mm});
            skLineSegment(sketch, "E413", {"start": v(-28.55, -2.67) * mm, "end": v(-27.21, -3.8) * mm});
            skLineSegment(sketch, "E414", {"start": v(-27.21, -3.8) * mm, "end": v(-25.73, -4.7) * mm});
            skLineSegment(sketch, "E415", {"start": v(-25.73, -4.7) * mm, "end": v(-24.54, -5.2) * mm});
            skLineSegment(sketch, "E416", {"start": v(-24.54, -5.2) * mm, "end": v(-24.13, -5.32) * mm});
            skLineSegment(sketch, "E417", {"start": v(-24.13, -5.32) * mm, "end": v(-23.73, -5.43) * mm});
            skLineSegment(sketch, "E418", {"start": v(-23.73, -5.43) * mm, "end": v(-22.52, -5.67) * mm});
            skLineSegment(sketch, "E419", {"start": v(-22.52, -5.67) * mm, "end": v(-20.92, -5.84) * mm});
            skLineSegment(sketch, "E420", {"start": v(-20.92, -5.84) * mm, "end": v(-19.32, -5.85) * mm});
            skLineSegment(sketch, "E421", {"start": v(-19.32, -5.85) * mm, "end": v(-17.72, -5.73) * mm});
            skLineSegment(sketch, "E422", {"start": v(-17.72, -5.73) * mm, "end": v(-16.13, -5.52) * mm});
            skLineSegment(sketch, "E423", {"start": v(-16.13, -5.52) * mm, "end": v(-14.54, -5.23) * mm});
            skLineSegment(sketch, "E424", {"start": v(-14.54, -5.23) * mm, "end": v(-12.95, -4.9) * mm});
            skLineSegment(sketch, "E425", {"start": v(-12.95, -4.9) * mm, "end": v(-11.75, -4.65) * mm});
            skLineSegment(sketch, "E426", {"start": v(-11.75, -4.65) * mm, "end": v(-11.35, -4.56) * mm});
            skLineSegment(sketch, "E427", {"start": v(-11.35, -4.56) * mm, "end": v(-10.5, -4.39) * mm});
            skLineSegment(sketch, "E428", {"start": v(-10.5, -4.39) * mm, "end": v(-7.94, -3.94) * mm});
            skLineSegment(sketch, "E429", {"start": v(-7.94, -3.94) * mm, "end": v(-4.56, -3.54) * mm});
            skLineSegment(sketch, "E430", {"start": v(-4.56, -3.54) * mm, "end": v(-1.16, -3.4) * mm});
            skLineSegment(sketch, "E431", {"start": v(-1.16, -3.4) * mm, "end": v(1.44, -3.52) * mm});
            skLineSegment(sketch, "E432", {"start": v(1.44, -3.52) * mm, "end": v(2.3, -3.62) * mm});
            skLineSegment(sketch, "E433", {"start": v(2.3, -3.62) * mm, "end": v(3.32, -3.73) * mm});
            skLineSegment(sketch, "E434", {"start": v(3.32, -3.73) * mm, "end": v(6.34, -4.17) * mm});
            skLineSegment(sketch, "E435", {"start": v(6.34, -4.17) * mm, "end": v(10.37, -4.8) * mm});
            skLineSegment(sketch, "E436", {"start": v(10.37, -4.8) * mm, "end": v(14.41, -5.35) * mm});
            skLineSegment(sketch, "E437", {"start": v(14.41, -5.35) * mm, "end": v(17.46, -5.6) * mm});
            skLineSegment(sketch, "E438", {"start": v(17.46, -5.6) * mm, "end": v(18.48, -5.64) * mm});
            skLineSegment(sketch, "E439", {"start": v(18.48, -5.64) * mm, "end": v(19.1, -5.65) * mm});
            skLineSegment(sketch, "E440", {"start": v(19.1, -5.65) * mm, "end": v(20.95, -5.63) * mm});
            skLineSegment(sketch, "E441", {"start": v(20.95, -5.63) * mm, "end": v(23.47, -5.47) * mm});
            skLineSegment(sketch, "E442", {"start": v(23.47, -5.47) * mm, "end": v(26, -5.15) * mm});
            skLineSegment(sketch, "E443", {"start": v(26, -5.15) * mm, "end": v(28.5, -4.66) * mm});
            skLineSegment(sketch, "E444", {"start": v(28.5, -4.66) * mm, "end": v(30.96, -3.98) * mm});
            skLineSegment(sketch, "E445", {"start": v(30.96, -3.98) * mm, "end": v(33.34, -3.1) * mm});
            skLineSegment(sketch, "E446", {"start": v(33.34, -3.1) * mm, "end": v(35.6, -2.02) * mm});
            skLineSegment(sketch, "E447", {"start": v(35.6, -2.02) * mm, "end": v(37.23, -1.07) * mm});
            skLineSegment(sketch, "E448", {"start": v(37.23, -1.07) * mm, "end": v(37.74, -0.72) * mm});
            skLineSegment(sketch, "E449", {"start": v(37.74, -0.72) * mm, "end": v(37.76, -0.7) * mm});
            skLineSegment(sketch, "E450", {"start": v(37.76, -0.7) * mm, "end": v(37.97, -0.56) * mm});
            skLineSegment(sketch, "E451", {"start": v(37.97, -0.56) * mm, "end": v(37.99, -0.55) * mm});
            skLineSegment(sketch, "E452", {"start": v(37.99, -0.55) * mm, "end": v(37.91, -0.6) * mm});
            skLineSegment(sketch, "E453", {"start": v(37.91, -0.6) * mm, "end": v(37.7, -0.72) * mm});
            skLineSegment(sketch, "E454", {"start": v(37.7, -0.72) * mm, "end": v(37.33, -0.92) * mm});
            skLineSegment(sketch, "E455", {"start": v(37.33, -0.92) * mm, "end": v(36.83, -1.18) * mm});
            skLineSegment(sketch, "E456", {"start": v(36.83, -1.18) * mm, "end": v(36.18, -1.49) * mm});
            skLineSegment(sketch, "E457", {"start": v(36.18, -1.49) * mm, "end": v(35.4, -1.83) * mm});
            skLineSegment(sketch, "E458", {"start": v(35.4, -1.83) * mm, "end": v(34.5, -2.2) * mm});
            skLineSegment(sketch, "E459", {"start": v(34.5, -2.2) * mm, "end": v(33.46, -2.57) * mm});
            skLineSegment(sketch, "E460", {"start": v(33.46, -2.57) * mm, "end": v(32.3, -2.94) * mm});
            skLineSegment(sketch, "E461", {"start": v(32.3, -2.94) * mm, "end": v(31, -3.3) * mm});
            skLineSegment(sketch, "E462", {"start": v(31, -3.3) * mm, "end": v(29.59, -3.64) * mm});
            skLineSegment(sketch, "E463", {"start": v(29.59, -3.64) * mm, "end": v(28.05, -3.94) * mm});
            skLineSegment(sketch, "E464", {"start": v(28.05, -3.94) * mm, "end": v(26.4, -4.19) * mm});
            skLineSegment(sketch, "E465", {"start": v(26.4, -4.19) * mm, "end": v(24.64, -4.37) * mm});
            skLineSegment(sketch, "E466", {"start": v(24.64, -4.37) * mm, "end": v(22.77, -4.49) * mm});
            skLineSegment(sketch, "E467", {"start": v(22.77, -4.49) * mm, "end": v(21.28, -4.52) * mm});
            skLineSegment(sketch, "E468", {"start": v(21.28, -4.52) * mm, "end": v(20.78, -4.51) * mm});
            skLineSegment(sketch, "E469", {"start": v(20.78, -4.51) * mm, "end": v(20.83, -4.5) * mm});
            skLineSegment(sketch, "E470", {"start": v(20.83, -4.5) * mm, "end": v(20.95, -4.42) * mm});
            skLineSegment(sketch, "E471", {"start": v(20.95, -4.42) * mm, "end": v(21.27, -4.22) * mm});
            skLineSegment(sketch, "E472", {"start": v(21.27, -4.22) * mm, "end": v(21.69, -3.9) * mm});
            skLineSegment(sketch, "E473", {"start": v(21.69, -3.9) * mm, "end": v(22.13, -3.47) * mm});
            skLineSegment(sketch, "E474", {"start": v(22.13, -3.47) * mm, "end": v(22.54, -2.92) * mm});
            skLineSegment(sketch, "E475", {"start": v(22.54, -2.92) * mm, "end": v(22.87, -2.25) * mm});
            skLineSegment(sketch, "E476", {"start": v(22.87, -2.25) * mm, "end": v(23.06, -1.46) * mm});
            skLineSegment(sketch, "E477", {"start": v(23.06, -1.46) * mm, "end": v(23.07, -0.77) * mm});
            skLineSegment(sketch, "E478", {"start": v(23.07, -0.77) * mm, "end": v(23.04, -0.55) * mm});
            skLineSegment(sketch, "E479", {"start": v(15.28, -1.25) * mm, "end": v(15.42, -1.16) * mm});
            skLineSegment(sketch, "E480", {"start": v(13.1, 4.78) * mm, "end": v(13.04, 4.88) * mm});
            skSolve(sketch);
        }
        {
            var Q0;
            Q0=makeQuery(id+"F0.imprint","IMPRINT",FACE,{"disambiguationData":[TD([[makeQuery(id+"F0.imprint","IMPRINT",EDGE,{"derivedFrom":sQuery(id+"F0.wireOp",EDGE,"E0")}),1.0]])]});
            extrude(context, id + "F1", {"entities" : qUnion([Q0]), "depth" : 3 * mm});
        }
    });
